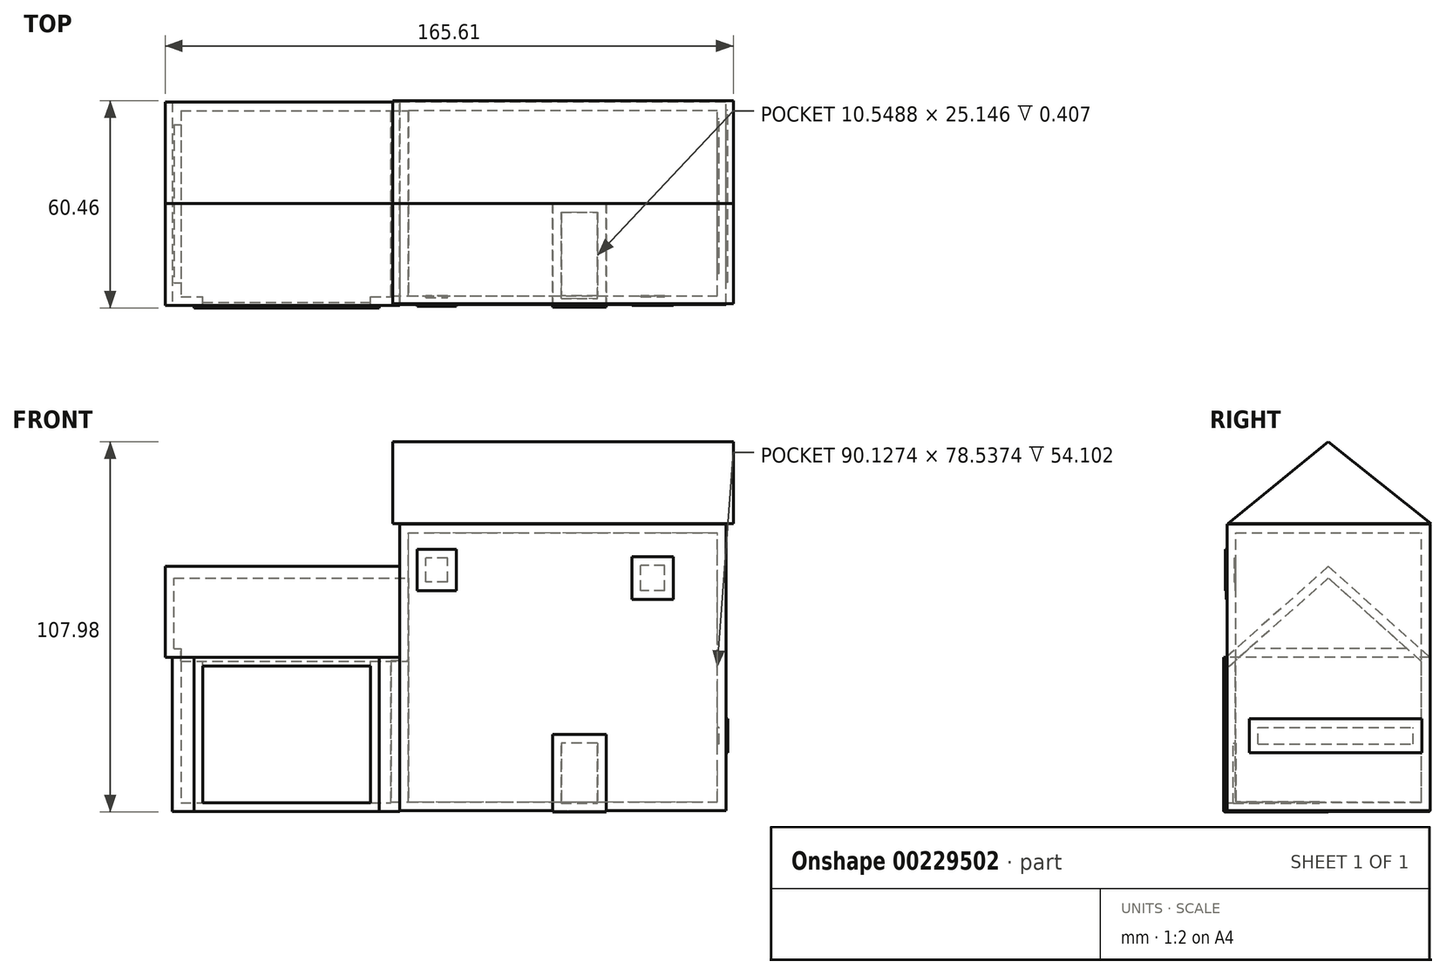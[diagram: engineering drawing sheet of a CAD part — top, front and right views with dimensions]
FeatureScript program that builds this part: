
annotation { "Feature Type Name" : "Feature", "Feature Type Description" : "" }
export const myFeature = defineFeature(function(context is Context, id is Id, definition is map)
    precondition{}
    {
        {
            var Q0;
            Q0=qCreatedBy(makeId("Right.planeOp"),FACE);
            var sketch = newSketch(context, id + "F0", { "sketchPlane" : qUnion([Q0])});
            skLineSegment(sketch, "E0", {"start": v(29.6, 0) * mm, "end": v(0, 26.55) * mm});
            skLineSegment(sketch, "E1", {"start": v(0, 26.55) * mm, "end": v(-29.78, 0) * mm});
            skLineSegment(sketch, "E2", {"start": v(29.6, 0) * mm, "end": v(-29.78, 0) * mm});
            skLineSegment(sketch, "E3.top", {"start": v(29.6, -44.86) * mm, "end": v(-29.78, -44.86) * mm});
            skLineSegment(sketch, "E3.left", {"start": v(29.6, 0) * mm, "end": v(29.6, -44.86) * mm});
            skLineSegment(sketch, "E3.right", {"start": v(-29.78, 0) * mm, "end": v(-29.78, -44.86) * mm});
            skSolve(sketch);
        }
        {
            var Q0;
            Q0 = qSketchRegion(id + "F0", true);
            extrude(context, id + "F1", {"entities" : qUnion([Q0]), "oppositeDirection" : true, "depth" : 66.3 * mm});
        }
        {
            var Q0;
            Q0=qCreatedBy(makeId("Front.planeOp"),FACE);
            var sketch = newSketch(context, id + "F2", { "sketchPlane" : qUnion([Q0])});
            skLineSegment(sketch, "E4.bottom", {"start": v(-59.94, 0) * mm, "end": v(-5.92, 0) * mm});
            skLineSegment(sketch, "E4.top", {"start": v(-59.94, -44.86) * mm, "end": v(-5.92, -44.86) * mm});
            skLineSegment(sketch, "E4.left", {"start": v(-59.94, 0) * mm, "end": v(-59.94, -44.86) * mm});
            skLineSegment(sketch, "E4.right", {"start": v(-5.92, 0) * mm, "end": v(-5.92, -44.86) * mm});
            skSolve(sketch);
        }
        {
            var Q0;
            Q0 = qSketchRegion(id + "F2", true);
            extrude(context, id + "F3", {"entities" : qUnion([Q0]), "operationType" : NewBodyOperationType.ADD, "depth" : 30.48 * mm});
        }
        {
            var Q0;
            Q0=qCreatedBy(makeId("Front.planeOp"),FACE);
            var sketch = newSketch(context, id + "F4", { "sketchPlane" : qUnion([Q0])});
            skLineSegment(sketch, "E5.bottom", {"start": v(0, -44.68) * mm, "end": v(50.5, -44.68) * mm});
            skLineSegment(sketch, "E5.top", {"start": v(0, 38.94) * mm, "end": v(50.5, 38.94) * mm});
            skLineSegment(sketch, "E5.left", {"start": v(0, -44.68) * mm, "end": v(0, 38.94) * mm});
            skLineSegment(sketch, "E5.right", {"start": v(50.5, -44.68) * mm, "end": v(50.5, 38.94) * mm});
            skSolve(sketch);
        }
        {
            var Q0;
            Q0 = qSketchRegion(id + "F4", true);
            extrude(context, id + "F5", {"entities" : qUnion([Q0]), "operationType" : NewBodyOperationType.ADD, "depth" : 29.46 * mm});
        }
        {
            var Q0;
            Q0=makeQuery(id+"F5.opExtrude","SWEPT_FACE",FACE,{"disambiguationData":[OSD([sQuery(id+"F4.wireOp",EDGE,"E5.right")])]});
            var sketch = newSketch(context, id + "F6", { "sketchPlane" : qUnion([Q0])});
            skSolve(sketch);
        }
        {
            var Q0;
            Q0=makeQuery(id+"F5.opExtrude","CAP_FACE",FACE,{"disambiguationData":[OSD([sQuery(id+"F4.wireOp",EDGE,"E5.bottom"),sQuery(id+"F4.wireOp",EDGE,"E5.top"),sQuery(id+"F4.wireOp",EDGE,"E5.left"),sQuery(id+"F4.wireOp",EDGE,"E5.right")])],"isStart":true});
            extrude(context, id + "F7", {"entities" : qUnion([Q0]), "operationType" : NewBodyOperationType.ADD, "depth" : 29.72 * mm});
        }
        {
            var Q0;
            {var subQ0=sQuery(id+"F4.wireOp",EDGE,"E5.right");Q0=makeQuery(id+"F6.imprint","IMPRINT",FACE,{"disambiguationData":[TD([[makeQuery(id+"F6.imprint","IMPRINT",EDGE,{"derivedFrom":makeQuery(id+"F5.opExtrude","CAP_EDGE",EDGE,{"disambiguationData":[OSD([subQ0])],"isStart":true})}),1.0]])]});}
            extrude(context, id + "F8", {"entities" : qUnion([Q0]), "operationType" : NewBodyOperationType.ADD, "depth" : 44.7 * mm});
        }
        {
            var Q0;
            {var subQ0=sQuery(id+"F4.wireOp",EDGE,"E5.right");Q0=makeQuery(id+"F7.boolean.opBoolean","MERGE",FACE,{"derivedFrom":[makeQuery(id+"F5.opExtrude","SWEPT_FACE",FACE,{"disambiguationData":[OSD([subQ0])]}),makeQuery(id+"F7.opExtrude","SWEPT_FACE",FACE,{"disambiguationData":[OSD([subQ0])]})]});}
            extrude(context, id + "F9", {"entities" : qUnion([Q0]), "operationType" : NewBodyOperationType.ADD, "depth" : 44.7 * mm});
        }
        {
            var Q0;
            Q0=qCreatedBy(makeId("Right.planeOp"),FACE);
            var sketch = newSketch(context, id + "F10", { "sketchPlane" : qUnion([Q0])});
            skLineSegment(sketch, "E6", {"start": v(-29.23, 38.76) * mm, "end": v(0, 63) * mm});
            skLineSegment(sketch, "E7", {"start": v(29.78, 38.78) * mm, "end": v(0, 63) * mm});
            skSolve(sketch);
        }
        {
            var Q0;
            Q0=sQuery(id+"F10.wireOp",EDGE,"E6");
            extrude(context, id + "F11", {"bodyType" : ToolBodyType.SURFACE, "surfaceEntities" : qUnion([Q0]), "depth" : 95.25 * mm});
        }
        {
            var Q0;
            Q0=qCreatedBy(makeId("Right.planeOp"),FACE);
            var sketch = newSketch(context, id + "F12", { "sketchPlane" : qUnion([Q0])});
            skLineSegment(sketch, "E8", {"start": v(29.34, 38.74) * mm, "end": v(0, 62.67) * mm});
            skSolve(sketch);
        }
        {
            var Q0;
            Q0=sQuery(id+"F12.wireOp",EDGE,"E8");
            extrude(context, id + "F13", {"bodyType" : ToolBodyType.SURFACE, "surfaceEntities" : qUnion([Q0]), "depth" : 95 * mm});
        }
        {
            var Q0;
            Q0=makeQuery(id+"F1.opExtrude","CAP_FACE",FACE,{"disambiguationData":[OSD([sQuery(id+"F0.wireOp",EDGE,"E0"),sQuery(id+"F0.wireOp",EDGE,"E1"),sQuery(id+"F0.wireOp",EDGE,"E3.top"),sQuery(id+"F0.wireOp",EDGE,"E3.left"),sQuery(id+"F0.wireOp",EDGE,"E3.right")])],"isStart":false});
            var sketch = newSketch(context, id + "F14", { "sketchPlane" : qUnion([Q0])});
            skLineSegment(sketch, "E9", {"start": v(-29.6, 0) * mm, "end": v(29.78, 0) * mm});
            skSolve(sketch);
        }
        {
            var Q0;
            Q0=qCreatedBy(makeId("Right.planeOp"),FACE);
            var sketch = newSketch(context, id + "F15", { "sketchPlane" : qUnion([Q0])});
            skLineSegment(sketch, "E10", {"start": v(-29.24, 39.08) * mm, "end": v(29.98, 39.08) * mm});
            skLineSegment(sketch, "E11", {"start": v(29.98, 39.08) * mm, "end": v(0, 62.9) * mm});
            skLineSegment(sketch, "E12", {"start": v(0, 62.9) * mm, "end": v(-29.24, 39.08) * mm});
            skSolve(sketch);
        }
        {
            var Q0;
            Q0=makeQuery(id+"F15.imprint","IMPRINT",FACE,{"disambiguationData":[TD([[makeQuery(id+"F15.imprint","IMPRINT",EDGE,{"derivedFrom":sQuery(id+"F15.wireOp",EDGE,"E10")}),1.0]])]});
            extrude(context, id + "F16", {"entities" : qUnion([Q0]), "depth" : 95.25 * mm});
        }
        {
            var Q0;
            Q0=qCreatedBy(makeId("Front.planeOp"),FACE);
            var sketch = newSketch(context, id + "F17", { "sketchPlane" : qUnion([Q0])});
            skLineSegment(sketch, "E13.bottom", {"start": v(5.09, 31.54) * mm, "end": v(16.55, 31.54) * mm});
            skLineSegment(sketch, "E13.top", {"start": v(5.09, 19.52) * mm, "end": v(16.55, 19.52) * mm});
            skLineSegment(sketch, "E13.left", {"start": v(5.09, 31.54) * mm, "end": v(5.09, 19.52) * mm});
            skLineSegment(sketch, "E13.right", {"start": v(16.55, 31.54) * mm, "end": v(16.55, 19.52) * mm});
            skSolve(sketch);
        }
        {
            var Q0;
            Q0=qCreatedBy(makeId("Front.planeOp"),FACE);
            var sketch = newSketch(context, id + "F18", { "sketchPlane" : qUnion([Q0])});
            skLineSegment(sketch, "E14.bottom", {"start": v(67.8, 29.32) * mm, "end": v(79.82, 29.32) * mm});
            skLineSegment(sketch, "E14.top", {"start": v(67.8, 16.93) * mm, "end": v(79.82, 16.93) * mm});
            skLineSegment(sketch, "E14.left", {"start": v(67.8, 29.32) * mm, "end": v(67.8, 16.93) * mm});
            skLineSegment(sketch, "E14.right", {"start": v(79.82, 29.32) * mm, "end": v(79.82, 16.93) * mm});
            skSolve(sketch);
        }
        {
            var Q0;
            Q0=makeQuery(id+"F18.imprint","IMPRINT",FACE,{"disambiguationData":[TD([[makeQuery(id+"F18.imprint","IMPRINT",EDGE,{"derivedFrom":sQuery(id+"F18.wireOp",EDGE,"E14.bottom")}),-1.0]])]});
            extrude(context, id + "F19", {"entities" : qUnion([Q0]), "operationType" : NewBodyOperationType.ADD, "depth" : 29.72 * mm});
        }
        {
            var Q0;
            Q0=makeQuery(id+"F17.imprint","IMPRINT",FACE,{"disambiguationData":[TD([[makeQuery(id+"F17.imprint","IMPRINT",EDGE,{"derivedFrom":sQuery(id+"F17.wireOp",EDGE,"E13.bottom")}),-1.0]])]});
            extrude(context, id + "F20", {"entities" : qUnion([Q0]), "operationType" : NewBodyOperationType.ADD, "depth" : 29.97 * mm});
        }
        {
            var Q0;
            Q0=qCreatedBy(makeId("Front.planeOp"),FACE);
            var sketch = newSketch(context, id + "F21", { "sketchPlane" : qUnion([Q0])});
            skLineSegment(sketch, "E15.bottom", {"start": v(44.58, -45.08) * mm, "end": v(60.21, -45.08) * mm});
            skLineSegment(sketch, "E15.top", {"start": v(44.58, -22.42) * mm, "end": v(60.21, -22.42) * mm});
            skLineSegment(sketch, "E15.left", {"start": v(44.58, -45.08) * mm, "end": v(44.58, -22.42) * mm});
            skLineSegment(sketch, "E15.right", {"start": v(60.21, -45.08) * mm, "end": v(60.21, -22.42) * mm});
            skSolve(sketch);
        }
        {
            var Q0;
            Q0=makeQuery(id+"F21.imprint","IMPRINT",FACE,{"disambiguationData":[TD([[makeQuery(id+"F21.imprint","IMPRINT",EDGE,{"derivedFrom":sQuery(id+"F21.wireOp",EDGE,"E15.bottom")}),1.0]])]});
            extrude(context, id + "F22", {"entities" : qUnion([Q0]), "operationType" : NewBodyOperationType.ADD, "depth" : 30.23 * mm});
        }
        {
            var Q0;
            Q0=qCreatedBy(makeId("Front.planeOp"),FACE);
            var sketch = newSketch(context, id + "F23", { "sketchPlane" : qUnion([Q0])});
            skLineSegment(sketch, "E16", {"start": v(10.63, 31.36) * mm, "end": v(10.63, 19.52) * mm});
            skSolve(sketch);
        }
        {
            var Q0;
            Q0=qCreatedBy(makeId("Front.planeOp"),FACE);
            var sketch = newSketch(context, id + "F24", { "sketchPlane" : qUnion([Q0])});
            skLineSegment(sketch, "E17", {"start": v(73.9, 29.33) * mm, "end": v(73.9, 16.86) * mm});
            skSolve(sketch);
        }
        {
            var Q0;
            Q0=sQuery(id+"F24.wireOp",EDGE,"E17");
            extrude(context, id + "F25", {"bodyType" : ToolBodyType.SURFACE, "surfaceEntities" : qUnion([Q0]), "depth" : 29.72 * mm});
        }
        {
            var Q0;
            Q0=sQuery(id+"F23.wireOp",EDGE,"E16");
            extrude(context, id + "F26", {"bodyType" : ToolBodyType.SURFACE, "surfaceEntities" : qUnion([Q0]), "depth" : 30.48 * mm});
        }
        {
            var Q0;
            Q0=makeQuery(id+"F14.imprint","IMPRINT",FACE,{"disambiguationData":[TD([[makeQuery(id+"F14.imprint","IMPRINT",EDGE,{"derivedFrom":sQuery(id+"F14.wireOp",EDGE,"E9")}),1.0]])]});
            extrude(context, id + "F27", {"entities" : qUnion([Q0]), "operationType" : NewBodyOperationType.ADD, "depth" : 2.03 * mm});
        }
        {
            var Q0;
            Q0=makeQuery(id+"F16.opExtrude","CAP_FACE",FACE,{"disambiguationData":[OSD([sQuery(id+"F15.wireOp",EDGE,"E10"),sQuery(id+"F15.wireOp",EDGE,"E11"),sQuery(id+"F15.wireOp",EDGE,"E12")])],"isStart":false});
            extrude(context, id + "F28", {"entities" : qUnion([Q0]), "operationType" : NewBodyOperationType.ADD, "depth" : 2.03 * mm});
        }
        {
            var Q0;
            Q0=makeQuery(id+"F16.opExtrude","CAP_FACE",FACE,{"disambiguationData":[OSD([sQuery(id+"F15.wireOp",EDGE,"E10"),sQuery(id+"F15.wireOp",EDGE,"E11"),sQuery(id+"F15.wireOp",EDGE,"E12")])],"isStart":true});
            extrude(context, id + "F29", {"entities" : qUnion([Q0]), "operationType" : NewBodyOperationType.ADD, "depth" : 2.03 * mm});
        }
        {
            var Q0;
            {var subQ0=sQuery(id+"F4.wireOp",EDGE,"E5.right");Q0=makeQuery(id+"F9.boolean.opBoolean","MERGE",FACE,{"derivedFrom":[makeQuery(id+"F8.opExtrude","CAP_FACE",FACE,{"disambiguationData":[OSD([sQuery(id+"F4.wireOp",EDGE,"E5.bottom"),sQuery(id+"F4.wireOp",EDGE,"E5.top"),subQ0])],"isStart":false}),makeQuery(id+"F9.opExtrude","CAP_FACE",FACE,{"disambiguationData":[OSD([subQ0])],"isStart":false})]});}
            var sketch = newSketch(context, id + "F30", { "sketchPlane" : qUnion([Q0])});
            skLineSegment(sketch, "E18.bottom", {"start": v(-23.01, -27.76) * mm, "end": v(27.22, -27.76) * mm});
            skLineSegment(sketch, "E18.top", {"start": v(-23.01, -17.85) * mm, "end": v(27.22, -17.85) * mm});
            skLineSegment(sketch, "E18.left", {"start": v(-23.01, -27.76) * mm, "end": v(-23.01, -17.85) * mm});
            skLineSegment(sketch, "E18.right", {"start": v(27.22, -27.76) * mm, "end": v(27.22, -17.85) * mm});
            skSolve(sketch);
        }
        {
            var Q0;
            Q0=makeQuery(id+"F30.imprint","IMPRINT",FACE,{"disambiguationData":[TD([[makeQuery(id+"F30.imprint","IMPRINT",EDGE,{"derivedFrom":sQuery(id+"F30.wireOp",EDGE,"E18.bottom")}),1.0]])]});
            extrude(context, id + "F31", {"entities" : qUnion([Q0]), "operationType" : NewBodyOperationType.ADD, "depth" : 0.5 * mm});
        }
        {
            var Q0;
            Q0=makeQuery(id+"F3.opExtrude","CAP_FACE",FACE,{"disambiguationData":[OSD([sQuery(id+"F2.wireOp",EDGE,"E4.bottom"),sQuery(id+"F2.wireOp",EDGE,"E4.top"),sQuery(id+"F2.wireOp",EDGE,"E4.left"),sQuery(id+"F2.wireOp",EDGE,"E4.right")])],"isStart":false});
            shell(context, id + "F32", {"entities" : qUnion([Q0]), "thickness" : 2.54 * mm});
        }
    });
